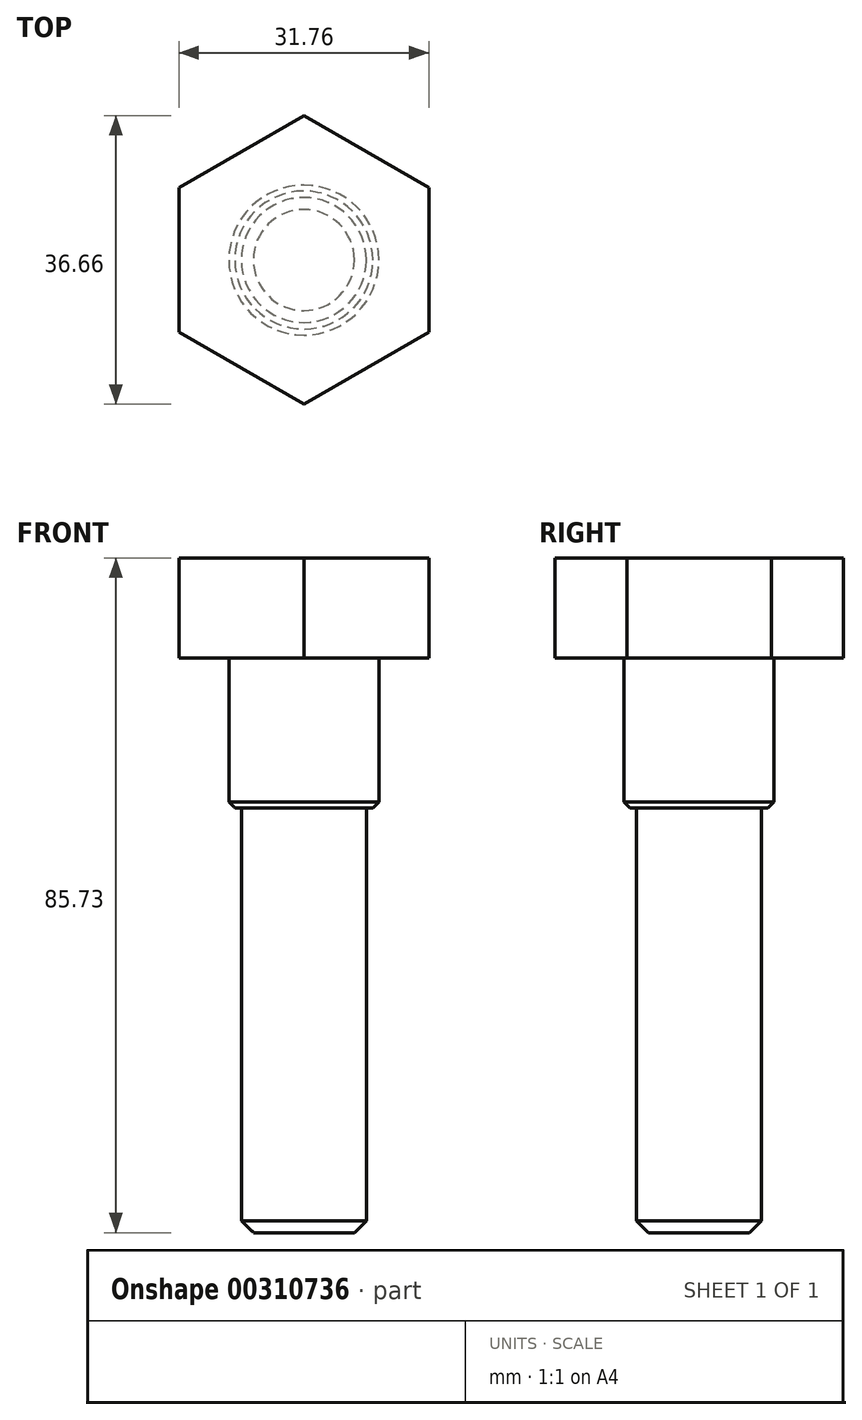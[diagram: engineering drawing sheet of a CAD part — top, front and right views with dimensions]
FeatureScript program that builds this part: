
annotation { "Feature Type Name" : "Feature", "Feature Type Description" : "" }
export const myFeature = defineFeature(function(context is Context, id is Id, definition is map)
    precondition{}
    {
        {
            var Q0;
            Q0=qCreatedBy(makeId("Top.planeOp"),FACE);
            var sketch = newSketch(context, id + "F0", { "sketchPlane" : qUnion([Q0])});
            skCircle(sketch, "E0.cCircle", {"center": v(0, 0) * mm, "radius": 15.88 * mm, "construction": true});
            skLineSegment(sketch, "E0.0", {"start": v(-15.88, -9.17) * mm, "end": v(-15.88, 9.17) * mm});
            skLineSegment(sketch, "E0.1", {"start": v(-15.88, 9.17) * mm, "end": v(0, 18.33) * mm});
            skLineSegment(sketch, "E0.2", {"start": v(0, 18.33) * mm, "end": v(15.87, 9.17) * mm});
            skLineSegment(sketch, "E0.3", {"start": v(15.87, 9.17) * mm, "end": v(15.88, -9.17) * mm});
            skLineSegment(sketch, "E0.4", {"start": v(15.88, -9.17) * mm, "end": v(0, -18.33) * mm});
            skLineSegment(sketch, "E0.5", {"start": v(0, -18.33) * mm, "end": v(-15.88, -9.17) * mm});
            skPoint(sketch, "E0.0.midPoint", {"position": v(-15.88, 0) * mm});
            skSolve(sketch);
        }
        {
            var Q0;
            Q0 = qSketchRegion(id + "F0", true);
            extrude(context, id + "F1", {"entities" : qUnion([Q0]), "depth" : 12.7 * mm});
        }
        {
            var Q0;
            Q0=makeQuery(id+"F1.opExtrude","CAP_FACE",FACE,{"disambiguationData":[OSD([sQuery(id+"F0.wireOp",EDGE,"E0.0"),sQuery(id+"F0.wireOp",EDGE,"E0.1"),sQuery(id+"F0.wireOp",EDGE,"E0.2"),sQuery(id+"F0.wireOp",EDGE,"E0.3"),sQuery(id+"F0.wireOp",EDGE,"E0.4"),sQuery(id+"F0.wireOp",EDGE,"E0.5")])],"isStart":true});
            var sketch = newSketch(context, id + "F2", { "sketchPlane" : qUnion([Q0])});
            skCircle(sketch, "E1", {"center": v(0, 0) * mm, "radius": 9.53 * mm});
            skSolve(sketch);
        }
        {
            var Q0;
            Q0 = qSketchRegion(id + "F2", true);
            extrude(context, id + "F3", {"entities" : qUnion([Q0]), "operationType" : NewBodyOperationType.ADD, "depth" : 19.05 * mm});
        }
        {
            var Q0;
            Q0=makeQuery(id+"F3.opExtrude","CAP_FACE",FACE,{"disambiguationData":[OSD([sQuery(id+"F2.wireOp",EDGE,"E1")])],"isStart":false});
            var sketch = newSketch(context, id + "F4", { "sketchPlane" : qUnion([Q0])});
            skCircle(sketch, "E2", {"center": v(0, 0) * mm, "radius": 7.94 * mm});
            skSolve(sketch);
        }
        {
            var Q0;
            Q0 = qSketchRegion(id + "F4", true);
            extrude(context, id + "F5", {"entities" : qUnion([Q0]), "operationType" : NewBodyOperationType.ADD, "depth" : 53.97 * mm});
        }
        {
            var Q0;
            Q0=makeQuery(id+"F5.opExtrude","CAP_FACE",FACE,{"disambiguationData":[OSD([sQuery(id+"F4.wireOp",EDGE,"E2")])],"isStart":false});
            chamfer(context, id + "F6", {"entities" : qUnion([Q0]), "width" : 1.52 * mm, "tangentPropagation" : true});
        }
        {
            var Q0;
            Q0=makeQuery(id+"F3.opExtrude","CAP_EDGE",EDGE,{"disambiguationData":[OSD([sQuery(id+"F2.wireOp",EDGE,"E1")])],"isStart":false});
            chamfer(context, id + "F7", {"entities" : qUnion([Q0]), "width" : 0.76 * mm, "tangentPropagation" : true});
        }
    });
